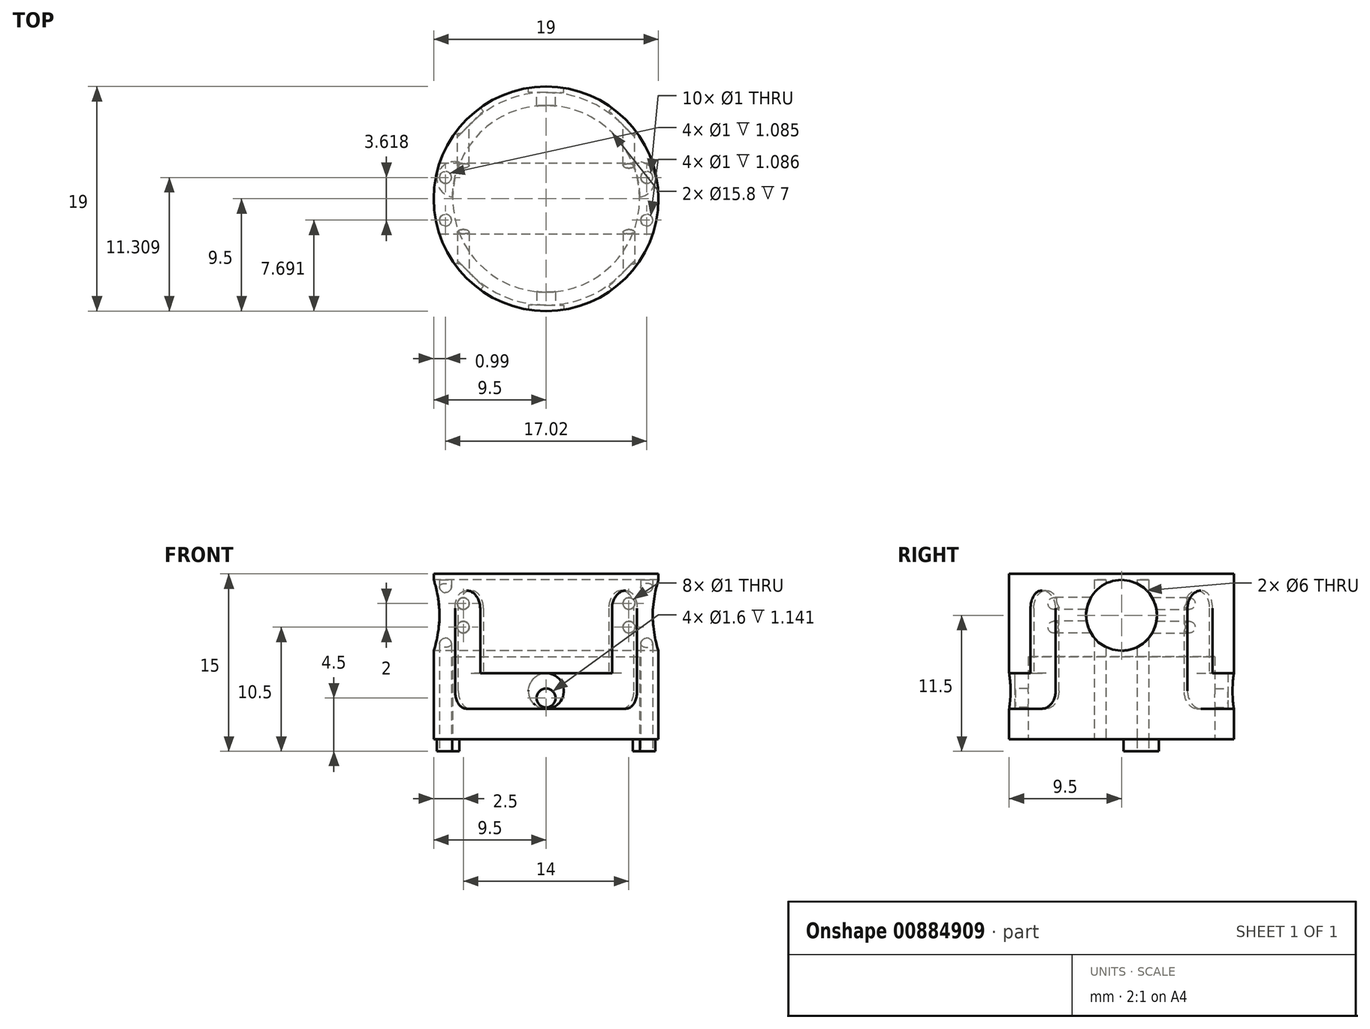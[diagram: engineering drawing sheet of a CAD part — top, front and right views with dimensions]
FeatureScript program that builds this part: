
annotation { "Feature Type Name" : "Feature", "Feature Type Description" : "" }
export const myFeature = defineFeature(function(context is Context, id is Id, definition is map)
    precondition{}
    {
        {
            var Q0;
            Q0=qCreatedBy(makeId("Top.planeOp"),FACE);
            var sketch = newSketch(context, id + "F0", { "sketchPlane" : qUnion([Q0])});
            skCircle(sketch, "E0", {"center": v(0, 0) * mm, "radius": 10 * mm});
            skSolve(sketch);
        }
        {
            var Q0;
            Q0=makeQuery(id+"F0.imprint","IMPRINT",FACE,{"disambiguationData":[TD([[makeQuery(id+"F0.imprint","IMPRINT",EDGE,{"derivedFrom":sQuery(id+"F0.wireOp",EDGE,"E0")}),1.0]])]});
            extrude(context, id + "F1", {"entities" : qUnion([Q0]), "depth" : 15 * mm, "offsetDistance" : 25 * mm});
        }
        {
            var Q0;
            Q0=makeQuery(id+"F1.opExtrude","CAP_FACE",FACE,{"disambiguationData":[OSD([sQuery(id+"F0.wireOp",EDGE,"E0")])],"isStart":false});
            var sketch = newSketch(context, id + "F2", { "sketchPlane" : qUnion([Q0])});
            skCircle(sketch, "E1", {"center": v(0, 0) * mm, "radius": 9.5 * mm});
            skSolve(sketch);
        }
        {
            var Q0;
            Q0=makeQuery(id+"F2.imprint","IMPRINT",FACE,{"disambiguationData":[TD([[makeQuery(id+"F2.imprint","IMPRINT",EDGE,{"derivedFrom":sQuery(id+"F2.wireOp",EDGE,"E1")}),1.0]])]});
            extrude(context, id + "F3", {"entities" : qUnion([Q0]), "operationType" : NewBodyOperationType.REMOVE, "oppositeDirection" : true, "depth" : 14 * mm, "offsetDistance" : 25 * mm});
        }
        {
            var Q0;
            Q0=makeQuery(id+"F1.opExtrude","CAP_FACE",FACE,{"disambiguationData":[OSD([sQuery(id+"F0.wireOp",EDGE,"E0")])],"isStart":true});
            var sketch = newSketch(context, id + "F4", { "sketchPlane" : qUnion([Q0])});
            skArc(sketch, "E2", {"start": v(3, -7.36) * mm, "mid": v(6.6, -4.44) * mm, "end": v(7.95, 0) * mm});
            skCircle(sketch, "E3", {"center": v(0, 0) * mm, "radius": 7.9 * mm, "construction": true});
            skArc(sketch, "E4", {"start": v(-1, -6.98) * mm, "mid": v(0, -7.05) * mm, "end": v(1, -6.98) * mm});
            skLineSegment(sketch, "E5.bottom", {"start": v(2, -9.8) * mm, "end": v(-2, -9.8) * mm, "construction": true});
            skLineSegment(sketch, "E5.top", {"start": v(2, 9.8) * mm, "end": v(-2, 9.8) * mm, "construction": true});
            skLineSegment(sketch, "E5.left", {"start": v(2, -9.8) * mm, "end": v(2, 9.8) * mm, "construction": true});
            skLineSegment(sketch, "E5.right", {"start": v(-2, -9.8) * mm, "end": v(-2, 9.8) * mm, "construction": true});
            skArc(sketch, "E6", {"start": v(1, -8) * mm, "mid": v(2, -9) * mm, "end": v(3, -8) * mm});
            skArc(sketch, "E7", {"start": v(-1, 8) * mm, "mid": v(-2, 9) * mm, "end": v(-3, 8) * mm});
            skLineSegment(sketch, "E8", {"start": v(1, -8) * mm, "end": v(1, -6.98) * mm});
            skLineSegment(sketch, "E9", {"start": v(-1, -8) * mm, "end": v(-1, -6.98) * mm});
            skLineSegment(sketch, "E10", {"start": v(3, -8) * mm, "end": v(3, -7.36) * mm});
            skLineSegment(sketch, "E11", {"start": v(-3, -8) * mm, "end": v(-3, -7.36) * mm});
            skLineSegment(sketch, "E12", {"start": v(3, 8) * mm, "end": v(3, 7.36) * mm});
            skLineSegment(sketch, "E13", {"start": v(1, 8) * mm, "end": v(1, 6.98) * mm});
            skLineSegment(sketch, "E14", {"start": v(-1, 8) * mm, "end": v(-1, 6.98) * mm});
            skLineSegment(sketch, "E15", {"start": v(-3, 8) * mm, "end": v(-3, 7.36) * mm});
            skArc(sketch, "E16.trimOffspring", {"start": v(1, 6.98) * mm, "mid": v(0, 7.05) * mm, "end": v(-1, 6.98) * mm});
            skArc(sketch, "E17.trimOffspring", {"start": v(-3, -8) * mm, "mid": v(-2, -9) * mm, "end": v(-1, -8) * mm});
            skArc(sketch, "E18.trimOffspring", {"start": v(3, 8) * mm, "mid": v(2, 9) * mm, "end": v(1, 8) * mm});
            skArc(sketch, "E19.trimOffspring", {"start": v(7.95, 0) * mm, "mid": v(6.6, 4.44) * mm, "end": v(3, 7.36) * mm});
            skArc(sketch, "E20.trimOffspring", {"start": v(-7.95, 0) * mm, "mid": v(-6.6, -4.44) * mm, "end": v(-3, -7.36) * mm});
            skArc(sketch, "E21.trimOffspring", {"start": v(-3, 7.36) * mm, "mid": v(-6.6, 4.44) * mm, "end": v(-7.95, 0) * mm});
            skSolve(sketch);
        }
        {
            var Q0;
            Q0=makeQuery(id+"F4.imprint","IMPRINT",FACE,{"disambiguationData":[TD([[makeQuery(id+"F4.imprint","IMPRINT",EDGE,{"derivedFrom":sQuery(id+"F4.wireOp",EDGE,"E2")}),1.0]])]});
            extrude(context, id + "F5", {"entities" : qUnion([Q0]), "operationType" : NewBodyOperationType.REMOVE, "endBound" : BoundingType.THROUGH_ALL, "oppositeDirection" : true, "depth" : 25 * mm, "offsetDistance" : 25 * mm});
        }
        {
            var Q0;
            Q0=qCreatedBy(makeId("Right.planeOp"),FACE);
            var sketch = newSketch(context, id + "F6", { "sketchPlane" : qUnion([Q0])});
            skCircle(sketch, "E22", {"center": v(0, 11.5) * mm, "radius": 3 * mm});
            skSolve(sketch);
        }
        {
            var Q0;
            Q0=makeQuery(id+"F6.imprint","IMPRINT",FACE,{"disambiguationData":[TD([[makeQuery(id+"F6.imprint","IMPRINT",EDGE,{"derivedFrom":sQuery(id+"F6.wireOp",EDGE,"E22")}),1.0]])]});
            extrude(context, id + "F7", {"entities" : qUnion([Q0]), "operationType" : NewBodyOperationType.REMOVE, "endBound" : BoundingType.SYMMETRIC, "oppositeDirection" : true, "depth" : 25 * mm, "offsetDistance" : 25 * mm});
        }
        {
            var Q0;
            Q0=makeQuery(id+"F1.opExtrude","CAP_FACE",FACE,{"disambiguationData":[OSD([sQuery(id+"F0.wireOp",EDGE,"E0")])],"isStart":true});
            var sketch = newSketch(context, id + "F8", { "sketchPlane" : qUnion([Q0])});
            skLineSegment(sketch, "E23", {"start": v(7.73, 1.64) * mm, "end": v(-7.73, -1.64) * mm, "construction": true});
            skArc(sketch, "E24", {"start": v(-7.33, -3.09) * mm, "mid": v(-9.2, -1.95) * mm, "end": v(-7.95, -0.16) * mm});
            skArc(sketch, "E25", {"start": v(7.95, 0.16) * mm, "mid": v(9.2, 1.95) * mm, "end": v(7.33, 3.09) * mm});
            skSolve(sketch);
        }
        {
            var Q0;
            {var subQ0=sQuery(id+"F8.wireOp",EDGE,"E24");Q0=makeQuery(id+"F8.imprint","IMPRINT",FACE,{"disambiguationData":[TD([[makeQuery(id+"F8.imprint","IMPRINT",EDGE,{"derivedFrom":subQ0}),-1.0]])]});}
            var Q1;
            {var subQ0=sQuery(id+"F8.wireOp",EDGE,"E25");Q1=makeQuery(id+"F8.imprint","IMPRINT",FACE,{"disambiguationData":[TD([[makeQuery(id+"F8.imprint","IMPRINT",EDGE,{"derivedFrom":subQ0}),1.0]])]});}
            extrude(context, id + "F9", {"entities" : qUnion([Q0, Q1]), "operationType" : NewBodyOperationType.REMOVE, "endBound" : BoundingType.THROUGH_ALL, "oppositeDirection" : true, "depth" : 25 * mm, "offsetDistance" : 25 * mm});
        }
        {
            var Q0;
            Q0=makeQuery(id+"F1.opExtrude","SWEPT_BODY",BODY,{"disambiguationData":[OSD([sQuery(id+"F0.wireOp",EDGE,"E0")])]});
            var Q1;
            Q1=qCreatedBy(makeId("Right.planeOp"),FACE);
            mirror(context, id + "F10", {"entities" : qUnion([Q0]), "mirrorPlane" : qUnion([Q1])});
        }
        {
            var Q0;
            Q0=qCreatedBy(makeId("Top.planeOp"),FACE);
            var sketch = newSketch(context, id + "F11", { "sketchPlane" : qUnion([Q0])});
            skCircle(sketch, "E26", {"center": v(0, 0) * mm, "radius": 9.5 * mm});
            skSolve(sketch);
        }
        {
            var Q0;
            Q0=makeQuery(id+"F11.imprint","IMPRINT",FACE,{"disambiguationData":[TD([[makeQuery(id+"F11.imprint","IMPRINT",EDGE,{"derivedFrom":sQuery(id+"F11.wireOp",EDGE,"E26")}),1.0]])]});
            extrude(context, id + "F12", {"entities" : qUnion([Q0]), "depth" : 14 * mm, "offsetDistance" : 25 * mm});
        }
        {
            var Q0;
            Q0=makeQuery(id+"F12.opExtrude","CAP_FACE",FACE,{"disambiguationData":[OSD([sQuery(id+"F11.wireOp",EDGE,"E26")])],"isStart":true});
            var sketch = newSketch(context, id + "F13", { "sketchPlane" : qUnion([Q0])});
            skCircle(sketch, "E27", {"center": v(0, 0) * mm, "radius": 7.9 * mm});
            skSolve(sketch);
        }
        {
            var Q0;
            Q0=makeQuery(id+"F13.imprint","IMPRINT",FACE,{"disambiguationData":[TD([[makeQuery(id+"F13.imprint","IMPRINT",EDGE,{"derivedFrom":sQuery(id+"F13.wireOp",EDGE,"E27")}),1.0]])]});
            extrude(context, id + "F14", {"entities" : qUnion([Q0]), "operationType" : NewBodyOperationType.REMOVE, "oppositeDirection" : true, "depth" : 7 * mm, "offsetDistance" : 25 * mm});
        }
        {
            var Q0;
            Q0=qCreatedBy(makeId("Right.planeOp"),FACE);
            var sketch = newSketch(context, id + "F15", { "sketchPlane" : qUnion([Q0])});
            skCircle(sketch, "E28", {"center": v(0, 10.5) * mm, "radius": 3 * mm});
            skSolve(sketch);
        }
        {
            var Q0;
            Q0 = qSketchRegion(id + "F15", true);
            var Q1;
            Q1=sQuery(id+"F15.wireOp",EDGE,"E28");
            extrude(context, id + "F16", {"entities" : qUnion([Q0]), "operationType" : NewBodyOperationType.REMOVE, "surfaceEntities" : qUnion([Q1]), "endBound" : BoundingType.SYMMETRIC, "depth" : 25 * mm, "offsetDistance" : 25 * mm});
        }
        {
            var Q0;
            Q0=qCreatedBy(makeId("Front.planeOp"),FACE);
            cPlane(context, id + "F17", {"entities" : qUnion([Q0]), "cplaneType" : CPlaneType.OFFSET, "offset" : (19 / 2) * mm, "width" : 150 * mm, "height" : 150 * mm});
        }
        {
            var Q0;
            Q0=qCreatedBy(id+"F17.planeOp",FACE);
            var sketch = newSketch(context, id + "F18", { "sketchPlane" : qUnion([Q0])});
            skCircle(sketch, "E29", {"center": v(0, 3.5) * mm, "radius": 0.8 * mm});
            skCircle(sketch, "E30", {"center": v(-7, 11.5) * mm, "radius": 0.5 * mm});
            skCircle(sketch, "E31", {"center": v(-7, 9.5) * mm, "radius": 0.5 * mm});
            skSolve(sketch);
        }
        {
            var Q0;
            Q0=makeQuery(id+"F18.imprint","IMPRINT",FACE,{"disambiguationData":[TD([[makeQuery(id+"F18.imprint","IMPRINT",EDGE,{"derivedFrom":sQuery(id+"F18.wireOp",EDGE,"E30")}),1.0]])]});
            var Q1;
            Q1=makeQuery(id+"F18.imprint","IMPRINT",FACE,{"disambiguationData":[TD([[makeQuery(id+"F18.imprint","IMPRINT",EDGE,{"derivedFrom":sQuery(id+"F18.wireOp",EDGE,"E31")}),1.0]])]});
            var Q2;
            Q2=makeQuery(id+"F18.imprint","IMPRINT",FACE,{"disambiguationData":[TD([[makeQuery(id+"F18.imprint","IMPRINT",EDGE,{"derivedFrom":sQuery(id+"F18.wireOp",EDGE,"E29")}),1.0]])]});
            extrude(context, id + "F19", {"entities" : qUnion([Q0, Q1, Q2]), "operationType" : NewBodyOperationType.REMOVE, "oppositeDirection" : true, "depth" : (19 / 2) * mm, "offsetDistance" : 25 * mm});
        }
        {
            var Q0;
            Q0=qCreatedBy(makeId("Front.planeOp"),FACE);
            cPlane(context, id + "F20", {"entities" : qUnion([Q0]), "cplaneType" : CPlaneType.OFFSET, "offset" : (19 / 2) * mm, "oppositeDirection" : true, "width" : 150 * mm, "height" : 150 * mm});
        }
        {
            var Q0;
            Q0=qCreatedBy(id+"F20.planeOp",FACE);
            var sketch = newSketch(context, id + "F21", { "sketchPlane" : qUnion([Q0])});
            skCircle(sketch, "E32", {"center": v(0, 3.5) * mm, "radius": 0.8 * mm});
            skCircle(sketch, "E33", {"center": v(7, 9.5) * mm, "radius": 0.5 * mm});
            skCircle(sketch, "E34", {"center": v(7, 11.5) * mm, "radius": 0.5 * mm});
            skCircle(sketch, "E35.0", {"center": v(-7, 11.5) * mm, "radius": 0.5 * mm});
            skCircle(sketch, "E36.0", {"center": v(-7, 9.5) * mm, "radius": 0.5 * mm});
            skSolve(sketch);
        }
        {
            var Q0;
            Q0=makeQuery(id+"F21.imprint","IMPRINT",FACE,{"disambiguationData":[TD([[makeQuery(id+"F21.imprint","IMPRINT",EDGE,{"derivedFrom":sQuery(id+"F21.wireOp",EDGE,"E33")}),1.0]])]});
            var Q1;
            Q1=makeQuery(id+"F21.imprint","IMPRINT",FACE,{"disambiguationData":[TD([[makeQuery(id+"F21.imprint","IMPRINT",EDGE,{"derivedFrom":sQuery(id+"F21.wireOp",EDGE,"E34")}),1.0]])]});
            var Q2;
            Q2=makeQuery(id+"F21.imprint","IMPRINT",FACE,{"disambiguationData":[TD([[makeQuery(id+"F21.imprint","IMPRINT",EDGE,{"derivedFrom":sQuery(id+"F21.wireOp",EDGE,"E32")}),1.0]])]});
            extrude(context, id + "F22", {"entities" : qUnion([Q0, Q1, Q2]), "operationType" : NewBodyOperationType.REMOVE, "depth" : (19 / 2) * mm, "offsetDistance" : 25 * mm});
        }
        {
            var Q0;
            Q0=qCreatedBy(id+"F17.planeOp",FACE);
            var sketch = newSketch(context, id + "F23", { "sketchPlane" : qUnion([Q0])});
            skCircle(sketch, "E37", {"center": v(0, 4.1) * mm, "radius": 1.5 * mm});
            skLineSegment(sketch, "E38", {"start": v(0, 2.6) * mm, "end": v(0, 5.6) * mm});
            skSolve(sketch);
        }
        {
            var Q0;
            Q0=qCreatedBy(makeId("Top.planeOp"),FACE);
            var sketch = newSketch(context, id + "F24", { "sketchPlane" : qUnion([Q0])});
            skLineSegment(sketch, "E39", {"start": v(-13.44, 0) * mm, "end": v(0, -13.44) * mm});
            skLineSegment(sketch, "E40", {"start": v(0, 13.44) * mm, "end": v(13.44, 0) * mm});
            skLineSegment(sketch, "E41", {"start": v(6.72, 6.72) * mm, "end": v(0, 0) * mm, "construction": true});
            skLineSegment(sketch, "E42", {"start": v(0, 0) * mm, "end": v(-6.72, -6.72) * mm, "construction": true});
            skSolve(sketch);
        }
        {
            var Q0;
            Q0=qCreatedBy(id+"F20.planeOp",FACE);
            var sketch = newSketch(context, id + "F25", { "sketchPlane" : qUnion([Q0])});
            skCircle(sketch, "E43", {"center": v(0, 4.1) * mm, "radius": 1.5 * mm});
            skLineSegment(sketch, "E44", {"start": v(0, 5.6) * mm, "end": v(0, 2.6) * mm});
            skSolve(sketch);
        }
        {
            var Q0;
            Q0=qCreatedBy(makeId("Front.planeOp"),FACE);
            var sketch = newSketch(context, id + "F26", { "sketchPlane" : qUnion([Q0])});
            skLineSegment(sketch, "E45", {"start": v(0, 0) * mm, "end": v(0, 30) * mm});
            skSolve(sketch);
        }
        {
            var Q0;
            Q0=sQuery(id+"F25.wireOp",EDGE,"E44");
            extrude(context, id + "F27", {"bodyType" : ToolBodyType.SURFACE, "surfaceEntities" : qUnion([Q0]), "depth" : 0.5 * mm, "offsetDistance" : 25 * mm});
        }
        {
            var Q0;
            Q0=makeQuery(id+"F27.opExtrude","SWEPT_FACE",FACE,{"disambiguationData":[OSD([sQuery(id+"F25.wireOp",EDGE,"E44")])]});
            var Q1;
            Q1=sQuery(id+"F26.wireOp",EDGE,"E45");
            revolve(context, id + "F28", {"operationType" : NewBodyOperationType.REMOVE, "surfaceOperationType" : NewSurfaceOperationType.NEW, "entities" : qUnion([Q0]), "axis" : qUnion([Q1]), "revolveType" : RevolveType.ONE_DIRECTION, "oppositeDirection" : true, "angle" : 45 * degree});
        }
        {
            var Q0;
            Q0=sQuery(id+"F23.wireOp",EDGE,"E38");
            extrude(context, id + "F29", {"bodyType" : ToolBodyType.SURFACE, "surfaceEntities" : qUnion([Q0]), "oppositeDirection" : true, "depth" : 0.5 * mm, "offsetDistance" : 25 * mm});
        }
        {
            var Q0;
            Q0=makeQuery(id+"F29.opExtrude","SWEPT_FACE",FACE,{"disambiguationData":[OSD([sQuery(id+"F23.wireOp",EDGE,"E38")])]});
            var Q1;
            Q1 = qSketchRegion(id + "F26", true);
            var Q2;
            Q2=sQuery(id+"F26.wireOp",EDGE,"E45");
            revolve(context, id + "F30", {"operationType" : NewBodyOperationType.REMOVE, "surfaceOperationType" : NewSurfaceOperationType.NEW, "entities" : qUnion([Q0, Q1]), "axis" : qUnion([Q2]), "revolveType" : RevolveType.ONE_DIRECTION, "oppositeDirection" : true, "angle" : 45 * degree});
        }
        {
            var Q0;
            {var subQ0=sQuery(id+"F23.wireOp",EDGE,"E38");Q0=makeQuery(id+"F23.imprint","IMPRINT",FACE,{"disambiguationData":[TD([[makeQuery(id+"F23.imprint","IMPRINT",EDGE,{"derivedFrom":subQ0}),-1.0]])]});}
            var Q1;
            {var subQ0=sQuery(id+"F23.wireOp",EDGE,"E38");Q1=makeQuery(id+"F23.imprint","IMPRINT",FACE,{"disambiguationData":[TD([[makeQuery(id+"F23.imprint","IMPRINT",EDGE,{"derivedFrom":subQ0}),1.0]])]});}
            extrude(context, id + "F31", {"entities" : qUnion([Q0, Q1]), "operationType" : NewBodyOperationType.REMOVE, "oppositeDirection" : true, "depth" : 0.5 * mm, "offsetDistance" : 25 * mm});
        }
        {
            var Q0;
            Q0=makeQuery(id+"F27.opExtrude","SWEPT_BODY",BODY,{"disambiguationData":[OSD([sQuery(id+"F25.wireOp",EDGE,"E44")])]});
            var Q1;
            Q1=makeQuery(id+"F29.opExtrude","SWEPT_BODY",BODY,{"disambiguationData":[OSD([sQuery(id+"F23.wireOp",EDGE,"E38")])]});
            deleteBodies(context, id + "F32", {"entities" : qUnion([Q0, Q1])});
        }
        {
            var Q0;
            {var subQ0=sQuery(id+"F25.wireOp",EDGE,"E44");Q0=makeQuery(id+"F25.imprint","IMPRINT",FACE,{"disambiguationData":[TD([[makeQuery(id+"F25.imprint","IMPRINT",EDGE,{"derivedFrom":subQ0}),-1.0]])]});}
            var Q1;
            {var subQ0=sQuery(id+"F25.wireOp",EDGE,"E44");Q1=makeQuery(id+"F25.imprint","IMPRINT",FACE,{"disambiguationData":[TD([[makeQuery(id+"F25.imprint","IMPRINT",EDGE,{"derivedFrom":subQ0}),1.0]])]});}
            extrude(context, id + "F33", {"entities" : qUnion([Q0, Q1]), "operationType" : NewBodyOperationType.REMOVE, "depth" : 0.5 * mm, "offsetDistance" : 25 * mm});
        }
        {
            var Q0;
            Q0=sQuery(id+"F24.wireOp",EDGE,"E40");
            var Q1;
            Q1=sQuery(id+"F24.wireOp",EDGE,"E39");
            extrude(context, id + "F34", {"bodyType" : ToolBodyType.SURFACE, "surfaceEntities" : qUnion([Q0, Q1]), "depth" : 25 * mm, "offsetDistance" : 25 * mm});
        }
        {
            var Q0;
            Q0=makeQuery(id+"F34.opExtrude","SWEPT_FACE",FACE,{"disambiguationData":[OSD([sQuery(id+"F24.wireOp",EDGE,"E40")])]});
            var sketch = newSketch(context, id + "F35", { "sketchPlane" : qUnion([Q0])});
            skLineSegment(sketch, "E46.0.0", {"start": v(-6.36, 4.3) * mm, "end": v(-6.36, 5.6) * mm});
            skLineSegment(sketch, "E46.0.1", {"start": v(-6.36, 5.6) * mm, "end": v(0, 5.6) * mm});
            skLineSegment(sketch, "E46.0.2", {"start": v(0, 5.6) * mm, "end": v(0, 2.6) * mm});
            skLineSegment(sketch, "E46.0.3", {"start": v(0, 2.6) * mm, "end": v(-6.36, 2.6) * mm});
            skLineSegment(sketch, "E46.0.4", {"start": v(-6.36, 2.6) * mm, "end": v(-6.36, 2.7) * mm});
            skFitSpline(sketch, "E46.0.5", {"points": [v(-6.36, 2.7) * mm, v(-6.29, 2.7) * mm, v(-6.14, 2.74) * mm, v(-5.94, 2.92) * mm, v(-5.8, 3.19) * mm, v(-5.76, 3.5) * mm, v(-5.8, 3.81) * mm, v(-5.94, 4.08) * mm, v(-6.14, 4.26) * mm, v(-6.29, 4.3) * mm, v(-6.36, 4.3) * mm]});
            skCircle(sketch, "E47", {"center": v(0, 4.1) * mm, "radius": 1.5 * mm});
            skCircle(sketch, "E48", {"center": v(0, 11.1) * mm, "radius": 1.5 * mm});
            skLineSegment(sketch, "E49", {"start": v(-1.5, 11.1) * mm, "end": v(-1.5, 4.1) * mm});
            skLineSegment(sketch, "E50", {"start": v(1.5, 4.1) * mm, "end": v(1.5, 11.1) * mm});
            skSolve(sketch);
        }
        {
            var Q0;
            {var subQ7=sQuery(id+"F35.wireOp",EDGE,"E50");Q0=makeQuery(id+"F35.imprint","IMPRINT",FACE,{"disambiguationData":[TD([[makeQuery(id+"F35.imprint","IMPRINT",EDGE,{"derivedFrom":subQ7}),1.0]])]});}
            var Q1;
            {var subQ0=sQuery(id+"F35.wireOp",EDGE,"E47");var subQ3=sQuery(id+"F35.wireOp",EDGE,"E49");var subQ5=makeQuery(id+"F35.imprint","INTERSECT",VERTEX,{"derivedFrom":[subQ0,subQ3]});Q1=makeQuery(id+"F35.imprint","IMPRINT",FACE,{"disambiguationData":[TD([[makeQuery(id+"F35.imprint","IMPRINT",EDGE,{"disambiguationData":[TD([[subQ5,1.0]])],"derivedFrom":subQ3}),1.0]])]});}
            var Q2;
            {var subQ0=sQuery(id+"F35.wireOp",EDGE,"E46.0.2");Q2=makeQuery(id+"F35.imprint","IMPRINT",FACE,{"disambiguationData":[TD([[makeQuery(id+"F35.imprint","IMPRINT",EDGE,{"derivedFrom":subQ0}),-1.0]])]});}
            var Q3;
            {var subQ0=sQuery(id+"F35.wireOp",EDGE,"E46.0.2");Q3=makeQuery(id+"F35.imprint","IMPRINT",FACE,{"disambiguationData":[TD([[makeQuery(id+"F35.imprint","IMPRINT",EDGE,{"derivedFrom":subQ0}),1.0]])]});}
            var Q4;
            {var subQ0=sQuery(id+"F35.wireOp",EDGE,"E48");var subQ1=makeQuery(id+"F35.imprint","INTERSECT",VERTEX,{"derivedFrom":[subQ0,sQuery(id+"F35.wireOp",EDGE,"E49")]});Q4=makeQuery(id+"F35.imprint","IMPRINT",FACE,{"disambiguationData":[TD([[makeQuery(id+"F35.imprint","IMPRINT",EDGE,{"disambiguationData":[TD([[subQ1,1.0]])],"derivedFrom":subQ0}),1.0]])]});}
            extrude(context, id + "F36", {"entities" : qUnion([Q0, Q1, Q2, Q3, Q4]), "operationType" : NewBodyOperationType.REMOVE, "depth" : 0.5 * mm, "offsetDistance" : 25 * mm});
        }
        {
            var Q0;
            Q0=makeQuery(id+"F34.opExtrude","SWEPT_FACE",FACE,{"disambiguationData":[OSD([sQuery(id+"F24.wireOp",EDGE,"E39")])]});
            var sketch = newSketch(context, id + "F37", { "sketchPlane" : qUnion([Q0])});
            skLineSegment(sketch, "E51.0.0", {"start": v(6.36, 4.3) * mm, "end": v(6.36, 5.6) * mm});
            skLineSegment(sketch, "E51.0.1", {"start": v(6.36, 5.6) * mm, "end": v(0, 5.6) * mm});
            skLineSegment(sketch, "E51.0.2", {"start": v(0, 5.6) * mm, "end": v(0, 2.6) * mm});
            skLineSegment(sketch, "E51.0.3", {"start": v(0, 2.6) * mm, "end": v(6.36, 2.6) * mm});
            skLineSegment(sketch, "E51.0.4", {"start": v(6.36, 2.6) * mm, "end": v(6.36, 2.7) * mm});
            skFitSpline(sketch, "E51.0.5", {"points": [v(6.36, 2.7) * mm, v(6.29, 2.7) * mm, v(6.14, 2.74) * mm, v(5.94, 2.92) * mm, v(5.8, 3.19) * mm, v(5.76, 3.5) * mm, v(5.8, 3.81) * mm, v(5.94, 4.08) * mm, v(6.14, 4.26) * mm, v(6.29, 4.3) * mm, v(6.36, 4.3) * mm]});
            skCircle(sketch, "E52", {"center": v(0, 4.1) * mm, "radius": 1.5 * mm});
            skCircle(sketch, "E53", {"center": v(0, 11.1) * mm, "radius": 1.5 * mm});
            skLineSegment(sketch, "E54", {"start": v(-1.5, 4.1) * mm, "end": v(-1.5, 11.1) * mm});
            skLineSegment(sketch, "E55", {"start": v(1.5, 11.1) * mm, "end": v(1.5, 4.1) * mm});
            skSolve(sketch);
        }
        {
            var Q0;
            {var subQ0=sQuery(id+"F37.wireOp",EDGE,"E53");var subQ1=makeQuery(id+"F37.imprint","INTERSECT",VERTEX,{"derivedFrom":[subQ0,sQuery(id+"F37.wireOp",EDGE,"E54")]});Q0=makeQuery(id+"F37.imprint","IMPRINT",FACE,{"disambiguationData":[TD([[makeQuery(id+"F37.imprint","IMPRINT",EDGE,{"disambiguationData":[TD([[subQ1,1.0]])],"derivedFrom":subQ0}),1.0]])]});}
            var Q1;
            {var subQ0=sQuery(id+"F37.wireOp",EDGE,"E54");Q1=makeQuery(id+"F37.imprint","IMPRINT",FACE,{"disambiguationData":[TD([[makeQuery(id+"F37.imprint","IMPRINT",EDGE,{"derivedFrom":subQ0}),-1.0]])]});}
            var Q2;
            {var subQ0=sQuery(id+"F37.wireOp",EDGE,"E52");var subQ3=sQuery(id+"F37.wireOp",EDGE,"E55");var subQ5=makeQuery(id+"F37.imprint","INTERSECT",VERTEX,{"derivedFrom":[subQ0,subQ3]});Q2=makeQuery(id+"F37.imprint","IMPRINT",FACE,{"disambiguationData":[TD([[makeQuery(id+"F37.imprint","IMPRINT",EDGE,{"disambiguationData":[TD([[subQ5,1.0]])],"derivedFrom":subQ3}),-1.0]])]});}
            var Q3;
            {var subQ0=sQuery(id+"F37.wireOp",EDGE,"E51.0.2");Q3=makeQuery(id+"F37.imprint","IMPRINT",FACE,{"disambiguationData":[TD([[makeQuery(id+"F37.imprint","IMPRINT",EDGE,{"derivedFrom":subQ0}),1.0]])]});}
            var Q4;
            {var subQ0=sQuery(id+"F37.wireOp",EDGE,"E51.0.2");Q4=makeQuery(id+"F37.imprint","IMPRINT",FACE,{"disambiguationData":[TD([[makeQuery(id+"F37.imprint","IMPRINT",EDGE,{"derivedFrom":subQ0}),-1.0]])]});}
            extrude(context, id + "F38", {"entities" : qUnion([Q0, Q1, Q2, Q3, Q4]), "operationType" : NewBodyOperationType.REMOVE, "oppositeDirection" : true, "depth" : 0.5 * mm, "offsetDistance" : 25 * mm});
        }
        {
            var Q0;
            Q0=makeQuery(id+"F12.opExtrude","SWEPT_BODY",BODY,{"disambiguationData":[OSD([sQuery(id+"F11.wireOp",EDGE,"E26")])]});
            var Q1;
            Q1=qCreatedBy(makeId("Right.planeOp"),FACE);
            mirror(context, id + "F39", {"entities" : qUnion([Q0]), "mirrorPlane" : qUnion([Q1])});
        }
        {
            var Q0;
            Q0=makeQuery(id+"F12.opExtrude","CAP_FACE",FACE,{"disambiguationData":[OSD([sQuery(id+"F11.wireOp",EDGE,"E26")])],"isStart":true});
            var sketch = newSketch(context, id + "F40", { "sketchPlane" : qUnion([Q0])});
            skLineSegment(sketch, "E56", {"start": v(-8.5, -1.8) * mm, "end": v(0, 0) * mm, "construction": true});
            skLineSegment(sketch, "E57", {"start": v(0, 0) * mm, "end": v(8.5, 1.8) * mm, "construction": true});
            skCircle(sketch, "E58", {"center": v(8.5, 1.8) * mm, "radius": 0.5 * mm});
            skCircle(sketch, "E59", {"center": v(-8.5, -1.8) * mm, "radius": 0.5 * mm});
            skSolve(sketch);
        }
        {
            var Q0;
            Q0=makeQuery(id+"F40.imprint","IMPRINT",FACE,{"disambiguationData":[TD([[makeQuery(id+"F40.imprint","IMPRINT",EDGE,{"derivedFrom":sQuery(id+"F40.wireOp",EDGE,"E58")}),1.0]])]});
            var Q1;
            Q1=makeQuery(id+"F40.imprint","IMPRINT",FACE,{"disambiguationData":[TD([[makeQuery(id+"F40.imprint","IMPRINT",EDGE,{"derivedFrom":sQuery(id+"F40.wireOp",EDGE,"E59")}),1.0]])]});
            extrude(context, id + "F41", {"entities" : qUnion([Q0, Q1]), "operationType" : NewBodyOperationType.REMOVE, "oppositeDirection" : true, "depth" : 13.5 * mm, "offsetDistance" : 25 * mm});
        }
        {
            var Q0;
            Q0=makeQuery(id+"F39.opPattern","COPY",FACE,{"derivedFrom":makeQuery(id+"F12.opExtrude","CAP_FACE",FACE,{"disambiguationData":[OSD([sQuery(id+"F11.wireOp",EDGE,"E26")])],"isStart":true}),"instanceName":"1"});
            var sketch = newSketch(context, id + "F42", { "sketchPlane" : qUnion([Q0])});
            skLineSegment(sketch, "E60", {"start": v(-8.5, 1.8) * mm, "end": v(0, 0) * mm, "construction": true});
            skLineSegment(sketch, "E61", {"start": v(0, 0) * mm, "end": v(8.5, -1.8) * mm, "construction": true});
            skCircle(sketch, "E62", {"center": v(-8.5, 1.8) * mm, "radius": 0.5 * mm});
            skCircle(sketch, "E63", {"center": v(8.5, -1.8) * mm, "radius": 0.5 * mm});
            skSolve(sketch);
        }
        {
            var Q0;
            Q0=makeQuery(id+"F42.imprint","IMPRINT",FACE,{"disambiguationData":[TD([[makeQuery(id+"F42.imprint","IMPRINT",EDGE,{"derivedFrom":sQuery(id+"F42.wireOp",EDGE,"E63")}),1.0]])]});
            var Q1;
            Q1=makeQuery(id+"F42.imprint","IMPRINT",FACE,{"disambiguationData":[TD([[makeQuery(id+"F42.imprint","IMPRINT",EDGE,{"derivedFrom":sQuery(id+"F42.wireOp",EDGE,"E62")}),1.0]])]});
            extrude(context, id + "F43", {"entities" : qUnion([Q0, Q1]), "operationType" : NewBodyOperationType.REMOVE, "oppositeDirection" : true, "depth" : 13.5 * mm, "offsetDistance" : 25 * mm});
        }
        {
            var Q0;
            Q0=makeQuery(id+"F12.opExtrude","SWEPT_BODY",BODY,{"disambiguationData":[OSD([sQuery(id+"F11.wireOp",EDGE,"E26")])]});
            var Q1;
            Q1=makeQuery(id+"F39.opPattern","COPY",BODY,{"derivedFrom":makeQuery(id+"F12.opExtrude","SWEPT_BODY",BODY,{"disambiguationData":[OSD([sQuery(id+"F11.wireOp",EDGE,"E26")])]}),"instanceName":"1"});
            transform(context, id + "F44", {"entities" : qUnion([Q0, Q1]), "transformType" : TransformType.TRANSLATION_3D, "dx" : 0 * mm, "dy" : 0 * mm, "dz" : 1 * mm, "makeCopy" : false});
        }
    });
